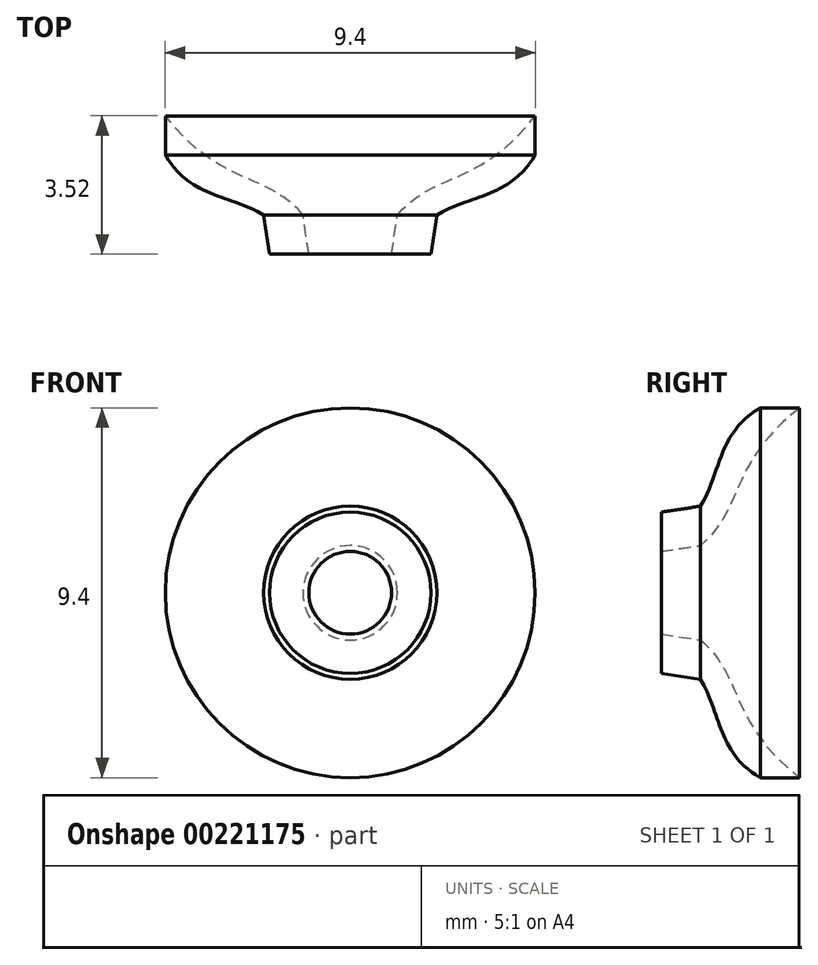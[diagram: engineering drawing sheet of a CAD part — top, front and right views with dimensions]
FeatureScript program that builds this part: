
annotation { "Feature Type Name" : "Feature", "Feature Type Description" : "" }
export const myFeature = defineFeature(function(context is Context, id is Id, definition is map)
    precondition{}
    {
        {
            var Q0;
            Q0=qCreatedBy(makeId("Top.planeOp"),FACE);
            var sketch = newSketch(context, id + "F0", { "sketchPlane" : qUnion([Q0])});
            skLineSegment(sketch, "E0", {"start": v(-4.7, 0) * mm, "end": v(4.7, 0) * mm, "construction": true});
            skLineSegment(sketch, "E1", {"start": v(-2.2, -2.4) * mm, "end": v(2.2, -2.4) * mm, "construction": true});
            skLineSegment(sketch, "E2", {"start": v(0, 2.24) * mm, "end": v(0, -13.4) * mm, "construction": true});
            skLineSegment(sketch, "E3", {"start": v(-2.05, -3.4) * mm, "end": v(2.05, -3.4) * mm, "construction": true});
            skPoint(sketch, "E4", {"position": v(0, -2.4) * mm});
            skSolve(sketch);
        }
        {
            var Q0;
            Q0=qCreatedBy(makeId("Top.planeOp"),FACE);
            var sketch = newSketch(context, id + "F1", { "sketchPlane" : qUnion([Q0])});
            skLineSegment(sketch, "E5", {"start": v(-2.05, -3.4) * mm, "end": v(-2.2, -2.4) * mm});
            skLineSegment(sketch, "E6", {"start": v(-2.05, -3.4) * mm, "end": v(-1.05, -3.4) * mm});
            skLineSegment(sketch, "E7", {"start": v(-1.05, -3.4) * mm, "end": v(-1.2, -2.4) * mm});
            skFitSpline(sketch, "E8", {"points": [v(-4.7, 0.12) * mm, v(-1.2, -2.4) * mm], "startDerivative": vector(4.2, -5.41) * mm, "endDerivative": vector(2.85, -3.34) * mm});
            skLineSegment(sketch, "E9", {"start": v(0, 0) * mm, "end": v(0, -5.13) * mm, "construction": true});
            skLineSegment(sketch, "E10", {"start": v(-4.7, 0.12) * mm, "end": v(-4.7, -0.88) * mm});
            skFitSpline(sketch, "E11", {"points": [v(-2.2, -2.4) * mm, v(-4.7, -0.88) * mm], "startDerivative": vector(-2.5, 1.52) * mm, "endDerivative": vector(-1.82, 3.2) * mm});
            skSolve(sketch);
        }
        {
            var Q0;
            Q0=qCreatedBy(makeId("Top.planeOp"),FACE);
            var sketch = newSketch(context, id + "F2", { "sketchPlane" : qUnion([Q0])});
            skLineSegment(sketch, "E12", {"start": v(0, 2.24) * mm, "end": v(0, -6.82) * mm, "construction": true});
            skSolve(sketch);
        }
        {
            var Q0;
            Q0 = qSketchRegion(id + "F1", true);
            var Q1;
            Q1=sQuery(id+"F2.wireOp",EDGE,"E12");
            revolve(context, id + "F3", {"entities" : qUnion([Q0]), "axis" : qUnion([Q1]), "revolveType" : RevolveType.FULL});
        }
    });
